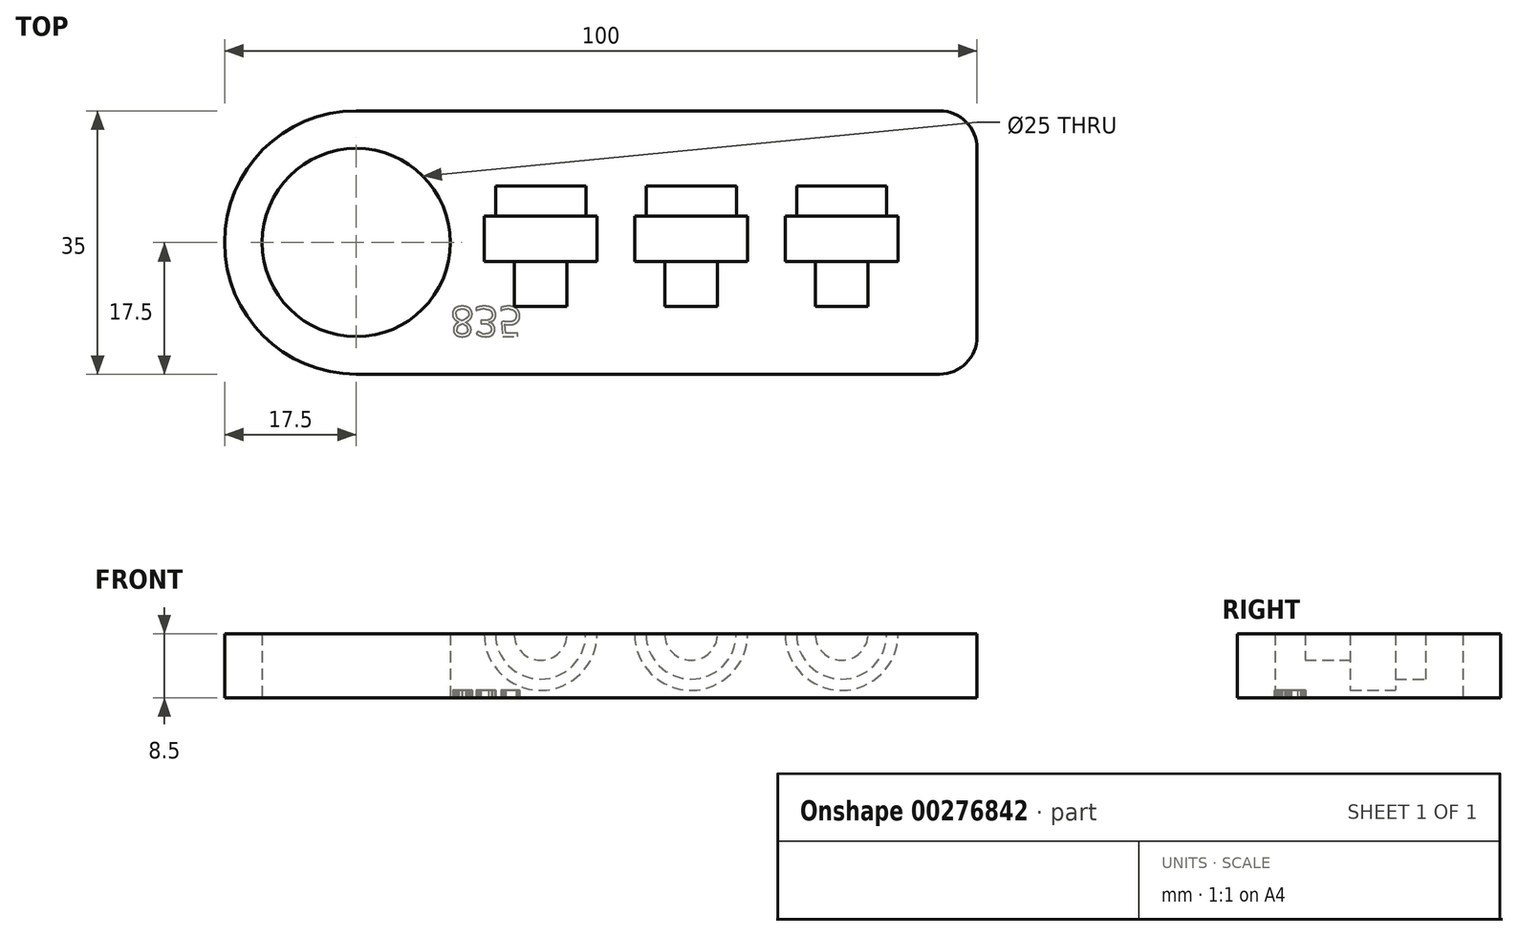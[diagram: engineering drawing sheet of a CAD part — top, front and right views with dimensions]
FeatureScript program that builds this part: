
annotation { "Feature Type Name" : "Feature", "Feature Type Description" : "" }
export const myFeature = defineFeature(function(context is Context, id is Id, definition is map)
    precondition{}
    {
        {
            var Q0;
            Q0=qCreatedBy(makeId("Top.planeOp"),FACE);
            var sketch = newSketch(context, id + "F0", { "sketchPlane" : qUnion([Q0])});
            skLineSegment(sketch, "E0.bottom", {"start": v(17.5, 0) * mm, "end": v(95, 0) * mm});
            skLineSegment(sketch, "E0.top", {"start": v(17.5, 35) * mm, "end": v(95, 35) * mm});
            skLineSegment(sketch, "E0.left", {"start": v(0, 17.5) * mm, "end": v(0, 17.5) * mm});
            skLineSegment(sketch, "E0.right", {"start": v(100, 5) * mm, "end": v(100, 30) * mm});
            skLineSegment(sketch, "E1.bottom", {"start": v(0, 0) * mm, "end": v(17.5, 0) * mm, "construction": true});
            skLineSegment(sketch, "E1.top", {"start": v(0, 17.5) * mm, "end": v(17.5, 17.5) * mm, "construction": true});
            skLineSegment(sketch, "E1.left", {"start": v(0, 0) * mm, "end": v(0, 17.5) * mm, "construction": true});
            skLineSegment(sketch, "E1.right", {"start": v(17.5, 0) * mm, "end": v(17.5, 17.5) * mm, "construction": true});
            skCircle(sketch, "E2", {"center": v(17.5, 17.5) * mm, "radius": 12.5 * mm});
            skPoint(sketch, "E3.visualSharp", {"position": v(0, 0) * mm});
            skArc(sketch, "E3.filletArc", {"start": v(0, 17.5) * mm, "mid": v(5.13, 5.13) * mm, "end": v(17.5, 0) * mm});
            skPoint(sketch, "E4.visualSharp", {"position": v(0, 35) * mm});
            skArc(sketch, "E4.filletArc", {"start": v(17.5, 35) * mm, "mid": v(5.13, 29.87) * mm, "end": v(0, 17.5) * mm});
            skPoint(sketch, "E5.visualSharp", {"position": v(100, 35) * mm});
            skArc(sketch, "E5.filletArc", {"start": v(100, 30) * mm, "mid": v(98.54, 33.54) * mm, "end": v(95, 35) * mm});
            skPoint(sketch, "E6.visualSharp", {"position": v(100, 0) * mm});
            skArc(sketch, "E6.filletArc", {"start": v(95, 0) * mm, "mid": v(98.54, 1.46) * mm, "end": v(100, 5) * mm});
            skSolve(sketch);
        }
        {
            var Q0;
            Q0=makeQuery(id+"F0.imprint","IMPRINT",FACE,{"disambiguationData":[TD([[makeQuery(id+"F0.imprint","IMPRINT",EDGE,{"derivedFrom":sQuery(id+"F0.wireOp",EDGE,"E0.bottom")}),1.0]])]});
            extrude(context, id + "F1", {"entities" : qUnion([Q0]), "depth" : 8.5 * mm});
        }
        {
            var Q0;
            Q0=makeQuery(id+"F1.opExtrude","CAP_FACE",FACE,{"disambiguationData":[OSD([sQuery(id+"F0.wireOp",EDGE,"E0.bottom"),sQuery(id+"F0.wireOp",EDGE,"E0.top"),sQuery(id+"F0.wireOp",EDGE,"E0.right"),sQuery(id+"F0.wireOp",EDGE,"E2"),sQuery(id+"F0.wireOp",EDGE,"E3.filletArc"),sQuery(id+"F0.wireOp",EDGE,"E4.filletArc"),sQuery(id+"F0.wireOp",EDGE,"E5.filletArc"),sQuery(id+"F0.wireOp",EDGE,"E6.filletArc")])],"isStart":false});
            var sketch = newSketch(context, id + "F2", { "sketchPlane" : qUnion([Q0])});
            skLineSegment(sketch, "E7.bottom", {"start": v(0, 0) * mm, "end": v(42, 0) * mm, "construction": true});
            skLineSegment(sketch, "E7.top", {"start": v(0, 9) * mm, "end": v(42, 9) * mm, "construction": true});
            skLineSegment(sketch, "E7.left", {"start": v(0, 0) * mm, "end": v(0, 9) * mm, "construction": true});
            skLineSegment(sketch, "E7.right", {"start": v(42, 0) * mm, "end": v(42, 9) * mm, "construction": true});
            skLineSegment(sketch, "E8", {"start": v(42, 9) * mm, "end": v(62, 9) * mm, "construction": true});
            skLineSegment(sketch, "E9", {"start": v(62, 9) * mm, "end": v(82, 9) * mm, "construction": true});
            skLineSegment(sketch, "E10.bottom", {"start": v(42, 9) * mm, "end": v(45.5, 9) * mm});
            skLineSegment(sketch, "E10.left", {"start": v(42, 9) * mm, "end": v(42, 15) * mm});
            skLineSegment(sketch, "E10.right", {"start": v(45.5, 9) * mm, "end": v(45.5, 15) * mm});
            skLineSegment(sketch, "E11.bottom", {"start": v(62, 9) * mm, "end": v(65.5, 9) * mm});
            skLineSegment(sketch, "E11.left", {"start": v(62, 9) * mm, "end": v(62, 15) * mm});
            skLineSegment(sketch, "E11.right", {"start": v(65.5, 9) * mm, "end": v(65.5, 15) * mm});
            skLineSegment(sketch, "E12.bottom", {"start": v(82, 9) * mm, "end": v(85.5, 9) * mm});
            skLineSegment(sketch, "E12.left", {"start": v(82, 9) * mm, "end": v(82, 15) * mm});
            skLineSegment(sketch, "E12.right", {"start": v(85.5, 9) * mm, "end": v(85.5, 15) * mm});
            skLineSegment(sketch, "E13.bottom", {"start": v(45.5, 15) * mm, "end": v(49.5, 15) * mm});
            skLineSegment(sketch, "E13.top", {"start": v(48, 21) * mm, "end": v(49.5, 21) * mm});
            skLineSegment(sketch, "E13.left", {"start": v(42, 15) * mm, "end": v(42, 21) * mm});
            skLineSegment(sketch, "E13.right", {"start": v(49.5, 15) * mm, "end": v(49.5, 21) * mm});
            skLineSegment(sketch, "E14.bottom", {"start": v(65.5, 15) * mm, "end": v(69.5, 15) * mm});
            skLineSegment(sketch, "E14.top", {"start": v(68, 21) * mm, "end": v(69.5, 21) * mm});
            skLineSegment(sketch, "E14.left", {"start": v(62, 15) * mm, "end": v(62, 21) * mm});
            skLineSegment(sketch, "E14.right", {"start": v(69.5, 15) * mm, "end": v(69.5, 21) * mm});
            skLineSegment(sketch, "E15.bottom", {"start": v(85.5, 15) * mm, "end": v(89.5, 15) * mm});
            skLineSegment(sketch, "E15.top", {"start": v(88, 21) * mm, "end": v(89.5, 21) * mm});
            skLineSegment(sketch, "E15.left", {"start": v(82, 15) * mm, "end": v(82, 21) * mm});
            skLineSegment(sketch, "E15.right", {"start": v(89.5, 15) * mm, "end": v(89.5, 21) * mm});
            skLineSegment(sketch, "E16.top", {"start": v(42, 25) * mm, "end": v(48, 25) * mm});
            skLineSegment(sketch, "E16.left", {"start": v(42, 21) * mm, "end": v(42, 25) * mm});
            skLineSegment(sketch, "E16.right", {"start": v(48, 21) * mm, "end": v(48, 25) * mm});
            skLineSegment(sketch, "E17.top", {"start": v(62, 25) * mm, "end": v(68, 25) * mm});
            skLineSegment(sketch, "E17.left", {"start": v(62, 21) * mm, "end": v(62, 25) * mm});
            skLineSegment(sketch, "E17.right", {"start": v(68, 21) * mm, "end": v(68, 25) * mm});
            skLineSegment(sketch, "E18.top", {"start": v(82, 25) * mm, "end": v(88, 25) * mm});
            skLineSegment(sketch, "E18.left", {"start": v(82, 21) * mm, "end": v(82, 25) * mm});
            skLineSegment(sketch, "E18.right", {"start": v(88, 21) * mm, "end": v(88, 25) * mm});
            skSolve(sketch);
        }
        {
            var Q0;
            Q0=makeQuery(id+"F2.imprint","IMPRINT",FACE,{"disambiguationData":[TD([[makeQuery(id+"F2.imprint","IMPRINT",EDGE,{"derivedFrom":sQuery(id+"F2.wireOp",EDGE,"E10.bottom")}),1.0]])]});
            var Q1;
            Q1=sQuery(id+"F2.wireOp",EDGE,"E13.left");
            revolve(context, id + "F3", {"operationType" : NewBodyOperationType.REMOVE, "entities" : qUnion([Q0]), "axis" : qUnion([Q1]), "revolveType" : RevolveType.FULL, "oppositeDirection" : true});
        }
        {
            var Q0;
            Q0=makeQuery(id+"F2.imprint","IMPRINT",FACE,{"disambiguationData":[TD([[makeQuery(id+"F2.imprint","IMPRINT",EDGE,{"derivedFrom":sQuery(id+"F2.wireOp",EDGE,"E11.bottom")}),1.0]])]});
            var Q1;
            Q1=sQuery(id+"F2.wireOp",EDGE,"E14.left");
            revolve(context, id + "F4", {"operationType" : NewBodyOperationType.REMOVE, "entities" : qUnion([Q0]), "axis" : qUnion([Q1]), "revolveType" : RevolveType.FULL, "oppositeDirection" : true});
        }
        {
            var Q0;
            Q0=makeQuery(id+"F2.imprint","IMPRINT",FACE,{"disambiguationData":[TD([[makeQuery(id+"F2.imprint","IMPRINT",EDGE,{"derivedFrom":sQuery(id+"F2.wireOp",EDGE,"E12.bottom")}),1.0]])]});
            var Q1;
            Q1=sQuery(id+"F2.wireOp",EDGE,"E15.left");
            revolve(context, id + "F5", {"operationType" : NewBodyOperationType.REMOVE, "entities" : qUnion([Q0]), "axis" : qUnion([Q1]), "revolveType" : RevolveType.FULL, "oppositeDirection" : true});
        }
        {
            var Q0;
            Q0=makeQuery(id+"F1.opExtrude","CAP_FACE",FACE,{"disambiguationData":[OSD([sQuery(id+"F0.wireOp",EDGE,"E0.bottom"),sQuery(id+"F0.wireOp",EDGE,"E0.top"),sQuery(id+"F0.wireOp",EDGE,"E0.right"),sQuery(id+"F0.wireOp",EDGE,"E2"),sQuery(id+"F0.wireOp",EDGE,"E3.filletArc"),sQuery(id+"F0.wireOp",EDGE,"E4.filletArc"),sQuery(id+"F0.wireOp",EDGE,"E5.filletArc"),sQuery(id+"F0.wireOp",EDGE,"E6.filletArc")])],"isStart":true});
            var sketch = newSketch(context, id + "F6", { "sketchPlane" : qUnion([Q0])});
            skLineSegment(sketch, "E19.bottom", {"start": v(0, 0) * mm, "end": v(30, 0) * mm, "construction": true});
            skLineSegment(sketch, "E19.top", {"start": v(0, -5) * mm, "end": v(30, -5) * mm, "construction": true});
            skLineSegment(sketch, "E19.left", {"start": v(0, 0) * mm, "end": v(0, -5) * mm, "construction": true});
            skLineSegment(sketch, "E19.right", {"start": v(30, 0) * mm, "end": v(30, -5) * mm, "construction": true});
            skText(sketch, "E20", { "text": "835", "fontName": "OpenSans-Regular.ttf"});
            const initialGuessF6  = {"E20": [0.03, -0.009, 1, 0, 0.004]};
            skSetInitialGuess(sketch, initialGuessF6);
            skSolve(sketch);
        }
        {
            var Q0;
            Q0 = qSketchRegion(id + "F6", true);
            extrude(context, id + "F7", {"entities" : qUnion([Q0]), "operationType" : NewBodyOperationType.REMOVE, "oppositeDirection" : true, "depth" : 1 * mm});
        }
    });
